# Revit family: Display_Mount-Wall-Vogels-PFS3504-Includes_Interface_Bar
name_source: partatom
category: Specialty Equipment
units: mm (PartAtom-declared; Revit-internal decimal feet)

## family parameters
Cut with Voids When Loaded = No
Host = Face
Part Type = Normal
Room Calculation Point = No
Round Connector Dimension = Use Diameter
Shared = No

## types (6) — shared parameters
Default Elevation = 48 "
Depth = 3.37 "
Description = Display Interface Strips, 3D Adjustable + Wall Mopunted Display Interface Bar
Height = 19.03 "
Manufacturer = Vogel´s
Product Material = Metal - Painted - Vogels - Black
URL = https://www.vogels.com
zero-valued in all types: Maximum Screen Size Inches, Minimum Screen Size Inches

## per-type parameters (varying)
| type | Maximum Weight Load | Model Bar | Width |
| PFS 3504 + PFB 3411 | 186 kg | Display_Mount-Wall-Vogels-Interface_Bar : PFB 3411 | 46.3 " |
| PFS 3504 + PFB 3407 | 260 kg | Display_Mount-Wall-Vogels-Interface_Bar : PFB 3407 | 28.1 " |
| PFS 3504 + PFB 3409 | 133 kg | Display_Mount-Wall-Vogels-Interface_Bar : PFB 3409 | 36 " |
| PFS 3504 + PFB 3419 | 240 kg | Display_Mount-Wall-Vogels-Interface_Bar : PFB 3419 | 75.4 " |
| PFS 3504 + PFB 3427 | 240 kg | Display_Mount-Wall-Vogels-Interface_Bar : PFB 3427 | 108.9 " |
| PFS 3504 + PFB 3433 | 240 kg | Display_Mount-Wall-Vogels-Interface_Bar : PFB 3433 | 130.5 " |

note: column(s) folded — value = type name in every type: Model

## geometry (parser evidence)
native form markers: Sweep x9
no freeform markers — native parametric forms only
